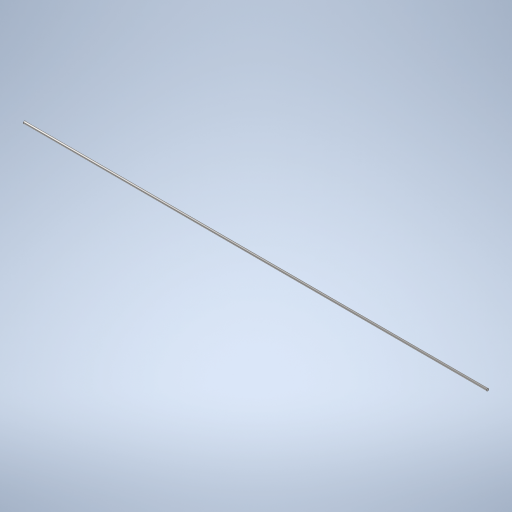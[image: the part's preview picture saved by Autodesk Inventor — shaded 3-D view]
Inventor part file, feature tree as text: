
AUTODESK INVENTOR PART (.ipt)
format: ipt  version: 2023 (Build 270158000, 158)  size: 238,592 bytes
history: native  units: mm
features: extrude x1, sketch x1
ambient origin geometry x8: Origin, YZ Plane, XZ Plane, XY Plane, X Axis, Y Axis, Z Axis, Center Point
bodies: Solid1 (feature_tree)
feature tree (2):
  extrude  "Extrusion1"  Depth=1000.0mm TaperAngle=0.0deg
  sketch  "Sketch1"  dims[d0=5.0mm d1=1000.0mm d2=0.0mm]
